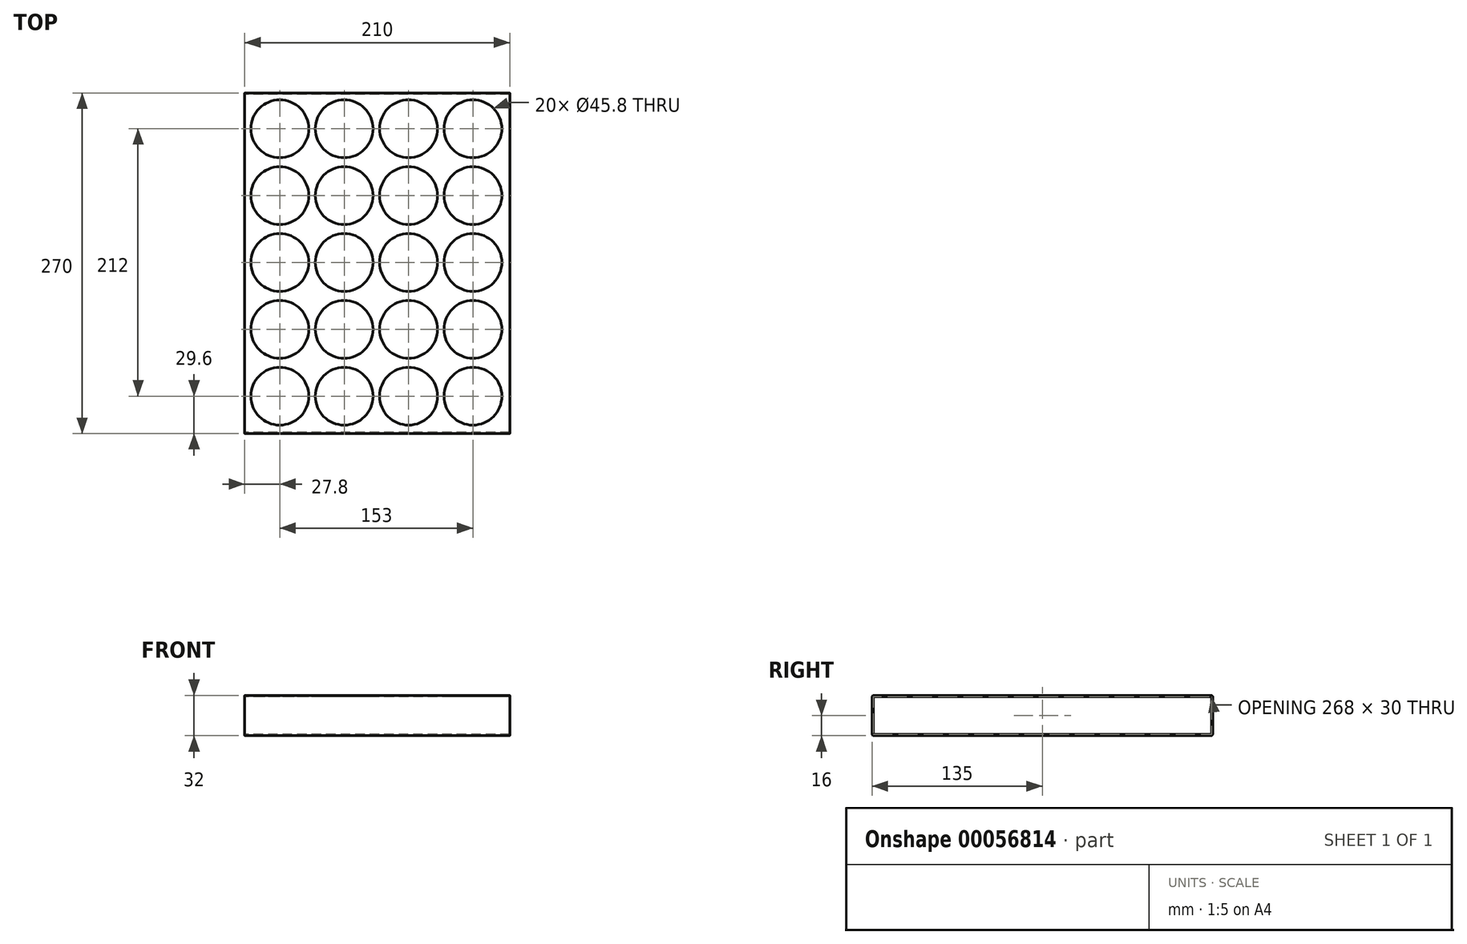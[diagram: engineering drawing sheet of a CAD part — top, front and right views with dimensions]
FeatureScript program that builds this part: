
annotation { "Feature Type Name" : "Feature", "Feature Type Description" : "" }
export const myFeature = defineFeature(function(context is Context, id is Id, definition is map)
    precondition{}
    {
        {
            var Q0;
            Q0=qCreatedBy(makeId("Right.planeOp"),FACE);
            var sketch = newSketch(context, id + "F0", { "sketchPlane" : qUnion([Q0])});
            skLineSegment(sketch, "E0.bottom", {"start": v(0, 0) * mm, "end": v(270, 0) * mm});
            skLineSegment(sketch, "E0.top", {"start": v(0, -32) * mm, "end": v(270, -32) * mm});
            skLineSegment(sketch, "E0.left", {"start": v(0, 0) * mm, "end": v(0, -32) * mm});
            skLineSegment(sketch, "E0.right", {"start": v(270, 0) * mm, "end": v(270, -32) * mm});
            skLineSegment(sketch, "E1.bottom", {"start": v(1, -1) * mm, "end": v(269, -1) * mm});
            skLineSegment(sketch, "E1.top", {"start": v(1, -31) * mm, "end": v(269, -31) * mm});
            skLineSegment(sketch, "E1.left", {"start": v(1, -1) * mm, "end": v(1, -31) * mm});
            skLineSegment(sketch, "E1.right", {"start": v(269, -1) * mm, "end": v(269, -31) * mm});
            skSolve(sketch);
        }
        {
            var Q0;
            Q0 = qSketchRegion(id + "F0", true);
            extrude(context, id + "F1", {"entities" : qUnion([Q0]), "depth" : 210 * mm});
        }
        {
            var Q0;
            Q0=makeQuery(id+"F1.opExtrude","SWEPT_FACE",FACE,{"disambiguationData":[OSD([sQuery(id+"F0.wireOp",EDGE,"E0.bottom")])]});
            var sketch = newSketch(context, id + "F2", { "sketchPlane" : qUnion([Q0])});
            skCircle(sketch, "E2", {"center": v(27.8, 29.6) * mm, "radius": 22.9 * mm});
            skCircle(sketch, "E3.0.1.0", {"center": v(27.8, 82.6) * mm, "radius": 22.9 * mm});
            skCircle(sketch, "E3.0.2.0", {"center": v(27.8, 135.6) * mm, "radius": 22.9 * mm});
            skCircle(sketch, "E3.0.3.0", {"center": v(27.8, 188.6) * mm, "radius": 22.9 * mm});
            skCircle(sketch, "E3.0.4.0", {"center": v(27.8, 241.6) * mm, "radius": 22.9 * mm});
            skCircle(sketch, "E3.1.0.0", {"center": v(78.8, 29.6) * mm, "radius": 22.9 * mm});
            skCircle(sketch, "E3.1.1.0", {"center": v(78.8, 82.6) * mm, "radius": 22.9 * mm});
            skCircle(sketch, "E3.1.2.0", {"center": v(78.8, 135.6) * mm, "radius": 22.9 * mm});
            skCircle(sketch, "E3.1.3.0", {"center": v(78.8, 188.6) * mm, "radius": 22.9 * mm});
            skCircle(sketch, "E3.1.4.0", {"center": v(78.8, 241.6) * mm, "radius": 22.9 * mm});
            skCircle(sketch, "E3.2.0.0", {"center": v(129.8, 29.6) * mm, "radius": 22.9 * mm});
            skCircle(sketch, "E3.2.1.0", {"center": v(129.8, 82.6) * mm, "radius": 22.9 * mm});
            skCircle(sketch, "E3.2.2.0", {"center": v(129.8, 135.6) * mm, "radius": 22.9 * mm});
            skCircle(sketch, "E3.2.3.0", {"center": v(129.8, 188.6) * mm, "radius": 22.9 * mm});
            skCircle(sketch, "E3.2.4.0", {"center": v(129.8, 241.6) * mm, "radius": 22.9 * mm});
            skCircle(sketch, "E3.3.0.0", {"center": v(180.8, 29.6) * mm, "radius": 22.9 * mm});
            skCircle(sketch, "E3.3.1.0", {"center": v(180.8, 82.6) * mm, "radius": 22.9 * mm});
            skCircle(sketch, "E3.3.2.0", {"center": v(180.8, 135.6) * mm, "radius": 22.9 * mm});
            skCircle(sketch, "E3.3.3.0", {"center": v(180.8, 188.6) * mm, "radius": 22.9 * mm});
            skCircle(sketch, "E3.3.4.0", {"center": v(180.8, 241.6) * mm, "radius": 22.9 * mm});
            skLineSegment(sketch, "E3.direction1", {"start": v(27.8, 29.6) * mm, "end": v(78.8, 29.6) * mm, "construction": true});
            skLineSegment(sketch, "E3.direction2", {"start": v(27.8, 29.6) * mm, "end": v(27.8, 82.6) * mm, "construction": true});
            skSolve(sketch);
        }
        {
            var Q0;
            Q0 = qSketchRegion(id + "F2", true);
            extrude(context, id + "F3", {"entities" : qUnion([Q0]), "operationType" : NewBodyOperationType.REMOVE, "endBound" : BoundingType.UP_TO_NEXT, "oppositeDirection" : true, "depth" : 25 * mm});
        }
        {
            var Q0;
            Q0=makeQuery(id+"F1.opExtrude","SWEPT_EDGE",EDGE,{"disambiguationData":[OSD([sQuery(id+"F0.wireOp",EDGE,"E0.bottom"),sQuery(id+"F0.wireOp",EDGE,"E0.right")])]});
            var Q1;
            Q1=makeQuery(id+"F1.opExtrude","SWEPT_EDGE",EDGE,{"disambiguationData":[OSD([sQuery(id+"F0.wireOp",EDGE,"E0.top"),sQuery(id+"F0.wireOp",EDGE,"E0.right")])]});
            var Q2;
            Q2=makeQuery(id+"F1.opExtrude","SWEPT_EDGE",EDGE,{"disambiguationData":[OSD([sQuery(id+"F0.wireOp",EDGE,"E0.top"),sQuery(id+"F0.wireOp",EDGE,"E0.left")])]});
            var Q3;
            Q3=makeQuery(id+"F1.opExtrude","SWEPT_EDGE",EDGE,{"disambiguationData":[OSD([sQuery(id+"F0.wireOp",EDGE,"E0.bottom"),sQuery(id+"F0.wireOp",EDGE,"E0.left")])]});
            fillet(context, id + "F4", {"entities" : qUnion([Q0, Q1, Q2, Q3]), "radius" : 1.5 * mm, "tangentPropagation" : true, "allowEdgeOverflow" : false});
        }
        {
            var Q0;
            Q0=makeQuery(id+"F1.opExtrude","SWEPT_EDGE",EDGE,{"disambiguationData":[OSD([sQuery(id+"F0.wireOp",EDGE,"E1.bottom"),sQuery(id+"F0.wireOp",EDGE,"E1.left")])]});
            var Q1;
            Q1=makeQuery(id+"F1.opExtrude","SWEPT_EDGE",EDGE,{"disambiguationData":[OSD([sQuery(id+"F0.wireOp",EDGE,"E1.top"),sQuery(id+"F0.wireOp",EDGE,"E1.left")])]});
            var Q2;
            Q2=makeQuery(id+"F1.opExtrude","SWEPT_EDGE",EDGE,{"disambiguationData":[OSD([sQuery(id+"F0.wireOp",EDGE,"E1.top"),sQuery(id+"F0.wireOp",EDGE,"E1.right")])]});
            var Q3;
            Q3=makeQuery(id+"F1.opExtrude","SWEPT_EDGE",EDGE,{"disambiguationData":[OSD([sQuery(id+"F0.wireOp",EDGE,"E1.bottom"),sQuery(id+"F0.wireOp",EDGE,"E1.right")])]});
            fillet(context, id + "F5", {"entities" : qUnion([Q0, Q1, Q2, Q3]), "radius" : 1 * mm, "tangentPropagation" : true, "allowEdgeOverflow" : false});
        }
    });
